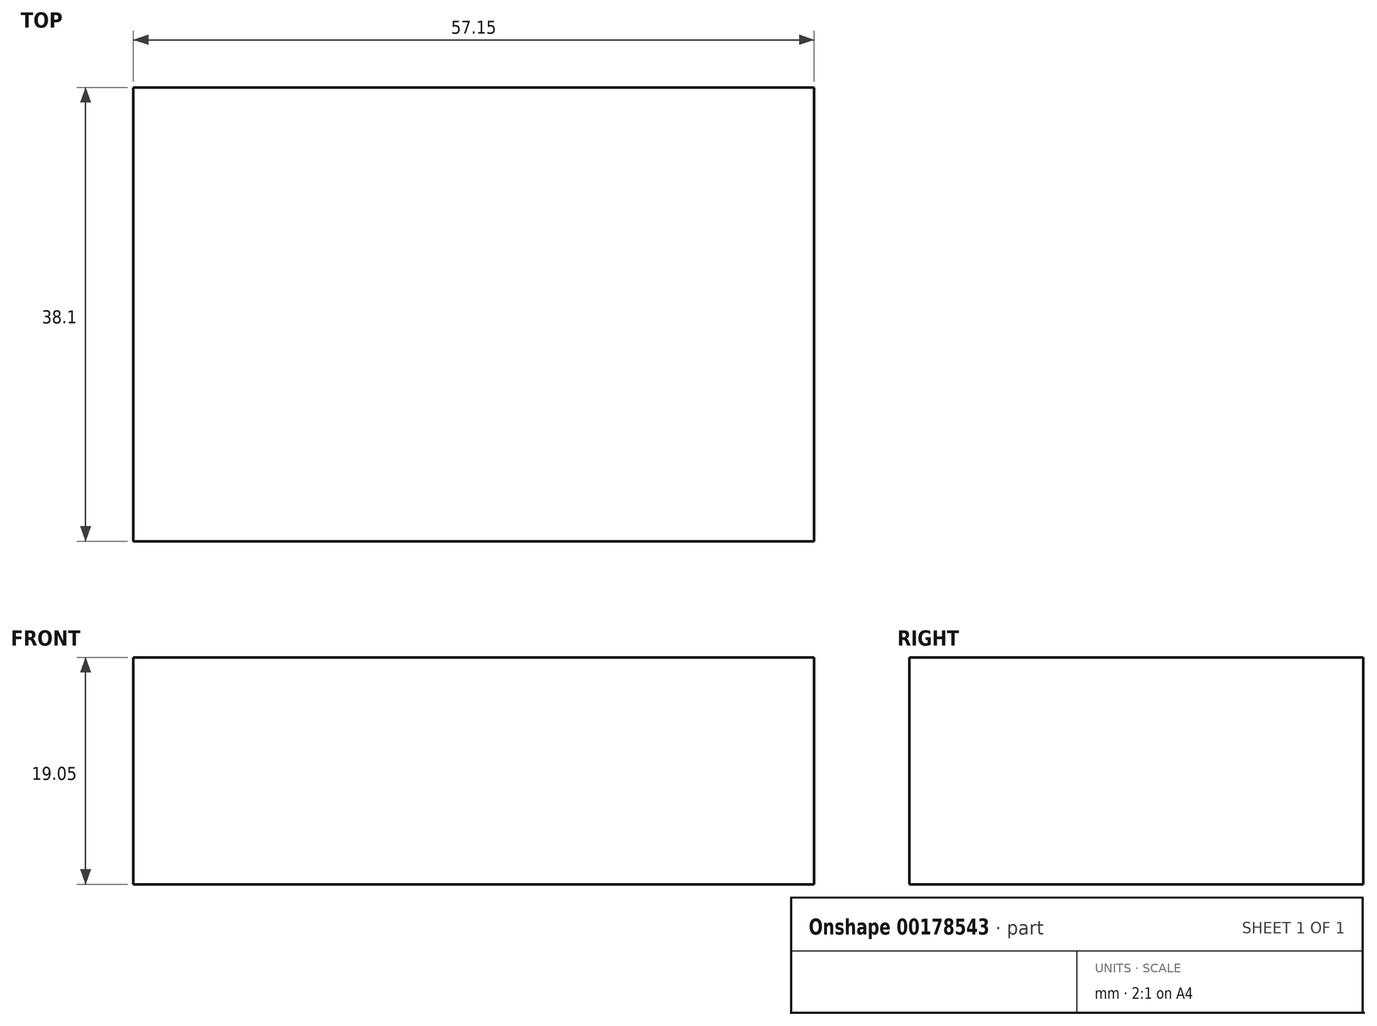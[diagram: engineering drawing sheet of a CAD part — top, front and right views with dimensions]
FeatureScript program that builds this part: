
annotation { "Feature Type Name" : "Feature", "Feature Type Description" : "" }
export const myFeature = defineFeature(function(context is Context, id is Id, definition is map)
    precondition{}
    {
        {
            var Q0;
            Q0=qCreatedBy(makeId("Front.planeOp"),FACE);
            var sketch = newSketch(context, id + "F0", { "sketchPlane" : qUnion([Q0])});
            skLineSegment(sketch, "E0.bottom", {"start": v(-64.48, 0) * mm, "end": v(-45.43, 0) * mm});
            skLineSegment(sketch, "E0.top", {"start": v(-64.48, 19.05) * mm, "end": v(-45.43, 19.05) * mm});
            skLineSegment(sketch, "E0.left", {"start": v(-64.48, 0) * mm, "end": v(-64.48, 19.05) * mm});
            skLineSegment(sketch, "E0.right", {"start": v(-45.43, 0) * mm, "end": v(-45.43, 19.05) * mm});
            skLineSegment(sketch, "E1.bottom", {"start": v(-45.43, 0) * mm, "end": v(-26.38, 0) * mm});
            skLineSegment(sketch, "E1.top", {"start": v(-45.43, 19.05) * mm, "end": v(-26.38, 19.05) * mm});
            skLineSegment(sketch, "E1.right", {"start": v(-26.38, 0) * mm, "end": v(-26.38, 19.05) * mm});
            skLineSegment(sketch, "E2.bottom", {"start": v(-26.38, 0) * mm, "end": v(-7.33, 0) * mm});
            skLineSegment(sketch, "E2.top", {"start": v(-26.38, 19.05) * mm, "end": v(-7.33, 19.05) * mm});
            skLineSegment(sketch, "E2.right", {"start": v(-7.33, 0) * mm, "end": v(-7.33, 19.05) * mm});
            skSolve(sketch);
        }
        {
            var Q0;
            Q0 = qSketchRegion(id + "F0", true);
            extrude(context, id + "F1", {"entities" : qUnion([Q0]), "oppositeDirection" : true, "depth" : 38.1 * mm});
        }
    });
